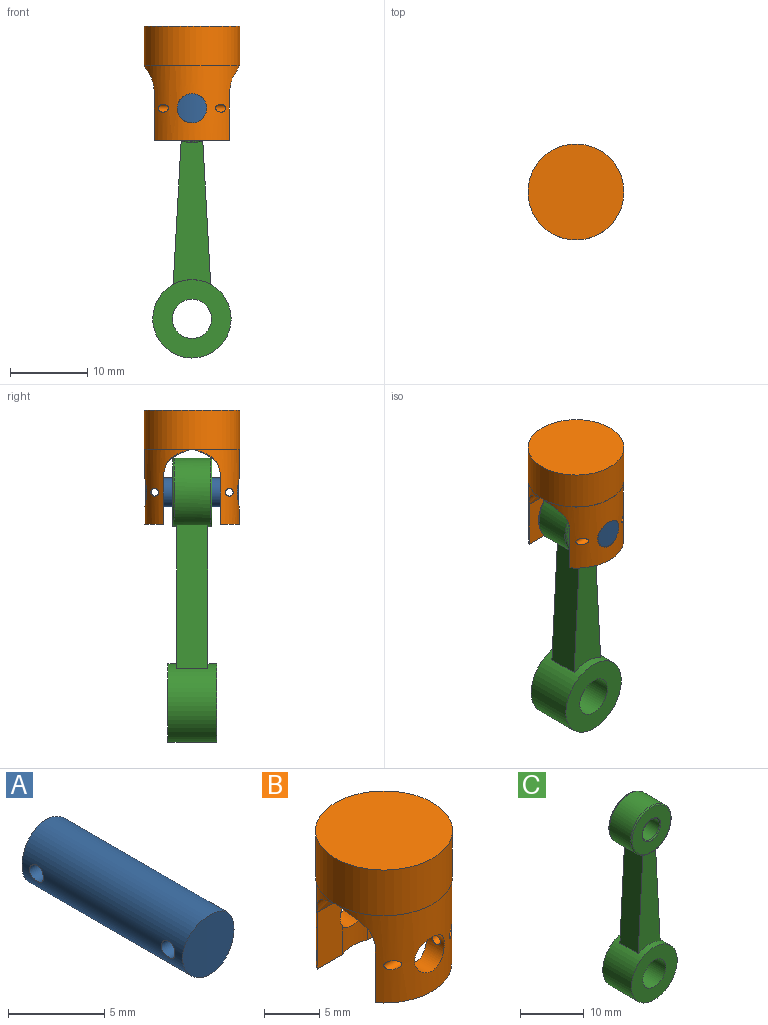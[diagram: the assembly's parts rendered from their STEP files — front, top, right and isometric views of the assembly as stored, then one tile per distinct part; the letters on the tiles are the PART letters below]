
ASSEMBLY  parts=3 mates=2
PART A: 5 faces, bbox 3.8x12.1x3.8 mm
  f0: cylinder r=1.89mm len=12.07mm, axis (0,1,0), area 138.5mm2, adj f1,f2,f3,f4
  f1: cylinder r=0.51mm len=3.78mm, axis (1,0,0), area 11.9mm2, adj f0
  f2: cylinder r=0.51mm len=3.78mm, axis (1,0,0), area 11.9mm2, adj f0
  f3: cylinder r=11.68mm len=3.79mm, axis (0,0,1), area 11.3mm2, adj f0
  f4: cylinder r=11.68mm len=3.79mm, axis (0,0,1), area 11.3mm2, adj f0
PART B: 24 faces, bbox 12.6x12.6x15 mm
  f0: cylinder r=6.14mm len=12.27mm, axis (0,0,1), area 102.9mm2, adj f1,f8,f10,f14,f17,f18,f20,f21
  f1: cylinder r=1.91mm len=3.81mm, axis (0,-1,0), area 24.1mm2, adj f0,f7,f9,f14,f17,f20,f21
  f2: revolved ~3.15x2.19mm, area 3.4mm2, adj f13,f15,f16,f19
  f3: cylinder r=6.14mm len=12.27mm, axis (0,0,1), area 102.9mm2, adj f4,f6,f10,f13,f15,f16,f19,f22
  f4: plane 9.73x2.4mm, normal (0,0,-1), area 15.5mm2, adj f3,f5,f13,f16
  f5: cylinder r=4.08mm len=3.25mm, axis (0,0,1), area 8.5mm2, adj f4,f13,f16,f19
  f6: plane 6.14x0.01mm, normal (0,1,0), area 0mm2, adj f3,f10,f15
  f7: revolved ~3.15x2.19mm, area 3.4mm2, adj f1,f14,f17,f18
  f8: plane 9.73x2.4mm, normal (0,0,-1), area 15.5mm2, adj f0,f9,f14,f17
  f9: cylinder r=4.08mm len=3.25mm, axis (0,0,1), area 8.5mm2, adj f1,f8,f14,f17
  f10: plane 12.45x12.45mm, normal (0,0,-1), area 3.4mm2, adj f0,f3,f6,f11,f18
  f11: cylinder r=6.22mm len=12.45mm, axis (0,0,-1), area 198.6mm2, adj f10,f12
  f12: plane 12.45x12.45mm, normal (0,0,1), area 121.7mm2, adj f11
  f13: plane 6.44x3.76mm, normal (0,1,0), area 20.3mm2, adj f2,f3,f4,f5,f15,f19
  f14: plane 6.44x3.76mm, normal (0,-1,0), area 20.3mm2, adj f0,f1,f7,f8,f9,f18
  f15: extruded ~12.27x3.74mm, area 58.9mm2, adj f2,f3,f6,f13,f16,f18
  f16: plane 6.44x3.76mm, normal (0,1,0), area 20.3mm2, adj f2,f3,f4,f5,f15,f19
  f17: plane 6.44x3.76mm, normal (0,-1,0), area 20.3mm2, adj f0,f1,f7,f8,f9,f18
  f18: extruded ~12.27x3.74mm, area 58.9mm2, adj f0,f7,f10,f14,f15,f17
  f19: cylinder r=1.91mm len=3.81mm, axis (0,-1,0), area 24.1mm2, adj f2,f3,f5,f13,f16,f22,f23
  f20: cylinder r=0.5mm len=2.52mm, axis (-1,0,0), area 6mm2, adj f0,f1
  f21: cylinder r=0.5mm len=2.52mm, axis (-1,0,0), area 6mm2, adj f0,f1
  f22: cylinder r=0.5mm len=2.52mm, axis (-1,0,0), area 6mm2, adj f3,f19
  f23: cylinder r=0.5mm len=2.52mm, axis (-1,0,0), area 6mm2, adj f3,f19
PART C: 16 faces, bbox 10.2x6.4x36.8 mm
  f0: plane 18.63x4.06mm, normal (1,0,0.06), area 75.8mm2, adj f3,f10,f11,f13
  f1: plane 18.63x4.06mm, normal (-1,0,0.06), area 75.8mm2, adj f3,f10,f11,f13
  f2: cylinder r=1.91mm len=4.71mm, axis (0,1,0), area 56.4mm2, adj f8,f9
  f3: cylinder r=4.45mm len=8.89mm, axis (0,1,0), area 120mm2, adj f0,f1,f6,f7,f10,f11
  f4: plane 8.54x8.53mm, normal (0,-1,0), area 43.3mm2, adj f6,f8
  f5: plane 8.54x8.53mm, normal (0,1,0), area 43.3mm2, adj f7,f9
  f6: bspline ~8.89x8.89mm, area 8.2mm2, adj f3,f4
  f7: bspline ~8.89x8.89mm, area 8.2mm2, adj f3,f5
  f8: bspline ~4.18x4.18mm, area 3.7mm2, adj f2,f4
  f9: bspline ~4.18x4.18mm, area 3.7mm2, adj f2,f5
  f10: plane 18.63x4.87mm, normal (0,-1,0), area 68.9mm2, adj f0,f1,f3,f13
  f11: plane 18.63x4.87mm, normal (0,1,0), area 68.9mm2, adj f0,f1,f3,f13
  f12: cylinder r=2.54mm len=6.35mm, axis (0,1,0), area 101.3mm2, adj f14,f15
  f13: cylinder r=5.08mm len=10.16mm, axis (0,1,0), area 182.1mm2, adj f0,f1,f10,f11,f14,f15
  f14: plane 10.16x10.16mm, normal (0,-1,0), area 60.8mm2, adj f12,f13
  f15: plane 10.16x10.16mm, normal (0,1,0), area 60.8mm2, adj f12,f13
PLACE A t=(-1.04,0.07,1.29)mm
PLACE B t=(-1.04,0.11,6.88)mm fixed
PLACE C t=(-1.04,0.07,-3.77)mm
MATE fastened B.f1 <-> A.f0  axis (0,-1,0) through (-1.04,-6.04,1.29)mm
MATE revolute C.f2 <-> A.f0  axis (0,1,0) through (-1.04,0.07,1.29)mm
